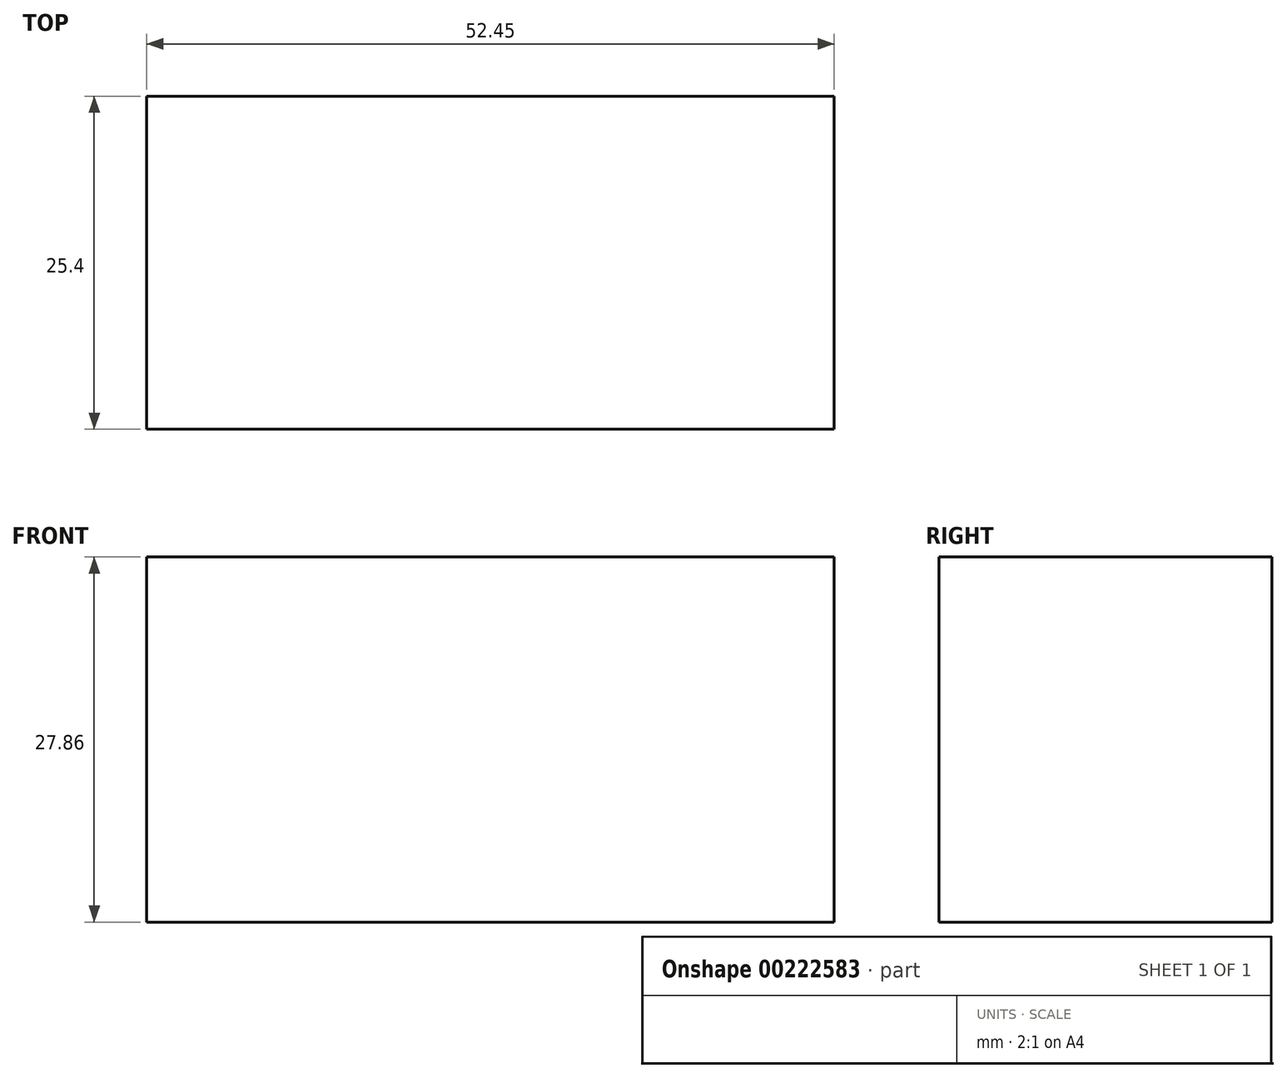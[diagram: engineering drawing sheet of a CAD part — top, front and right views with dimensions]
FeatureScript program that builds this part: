
annotation { "Feature Type Name" : "Feature", "Feature Type Description" : "" }
export const myFeature = defineFeature(function(context is Context, id is Id, definition is map)
    precondition{}
    {
        {
            var Q0;
            Q0=qCreatedBy(makeId("Front.planeOp"),FACE);
            var sketch = newSketch(context, id + "F0", { "sketchPlane" : qUnion([Q0])});
            skLineSegment(sketch, "E0.bottom", {"start": v(0, 0) * mm, "end": v(52.45, 0) * mm});
            skLineSegment(sketch, "E0.top", {"start": v(0, 27.86) * mm, "end": v(52.45, 27.86) * mm});
            skLineSegment(sketch, "E0.left", {"start": v(0, 0) * mm, "end": v(0, 27.86) * mm});
            skLineSegment(sketch, "E0.right", {"start": v(52.45, 0) * mm, "end": v(52.45, 27.86) * mm});
            skSolve(sketch);
        }
        {
            var Q0;
            Q0=makeQuery(id+"F0.imprint","IMPRINT",FACE,{"disambiguationData":[TD([[makeQuery(id+"F0.imprint","IMPRINT",EDGE,{"derivedFrom":sQuery(id+"F0.wireOp",EDGE,"E0.bottom")}),1.0]])]});
            extrude(context, id + "F1", {"entities" : qUnion([Q0]), "depth" : 25.4 * mm});
        }
    });
